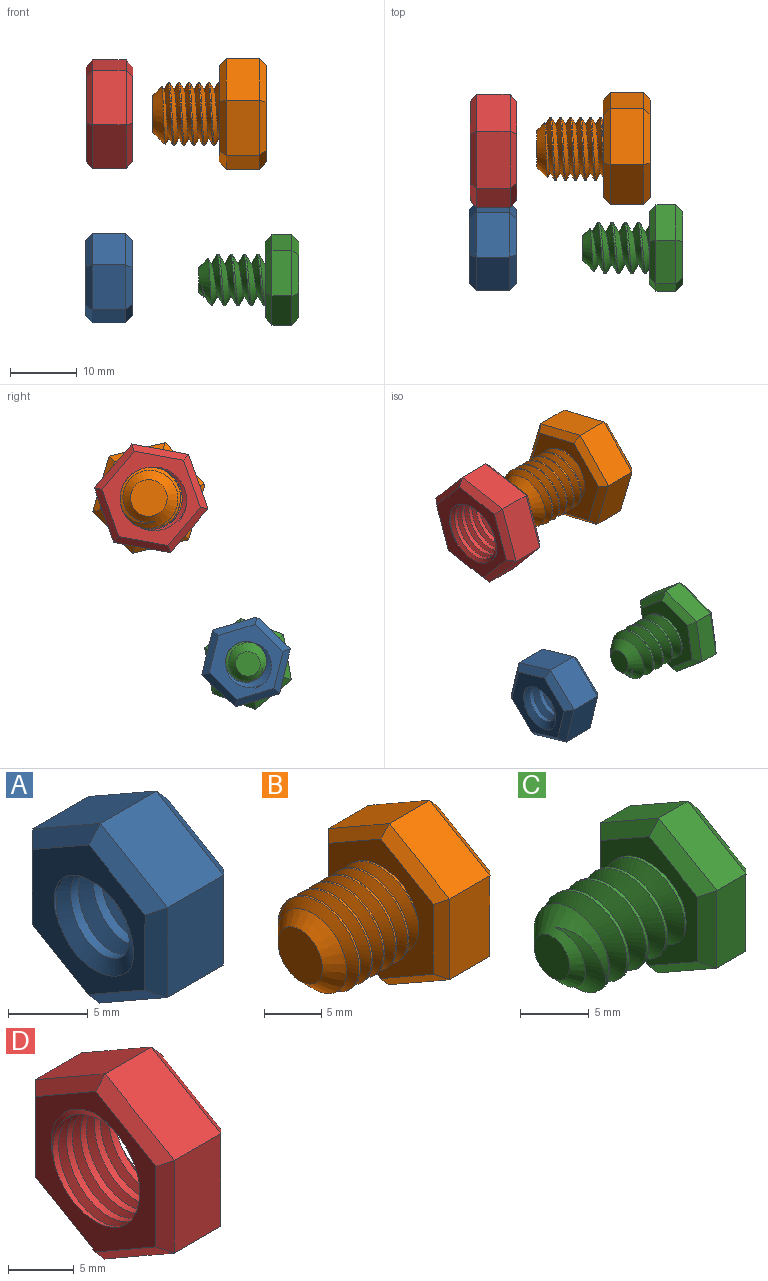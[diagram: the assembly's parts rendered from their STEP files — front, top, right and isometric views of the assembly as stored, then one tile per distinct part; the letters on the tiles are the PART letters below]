
ASSEMBLY  parts=4 mates=2
PART A: 23 faces, bbox 9.2x12.6x14.4 mm
  f0: cylinder r=3.08mm len=7mm, axis (1,0,0), area 47.4mm2, adj f7,f8,f21,f22
  f1: plane 6.02x5mm, normal (0,0.5,0.87), area 34.6mm2, adj f2,f6,f13,f20
  f2: plane 5.98x5mm, normal (0,-0.5,0.86), area 34.6mm2, adj f1,f3,f14,f18
  f3: plane 6.93x5mm, normal (0,-1,-0.01), area 34.6mm2, adj f2,f4,f12,f16
  f4: plane 6.02x5mm, normal (0,-0.5,-0.87), area 34.6mm2, adj f3,f5,f10,f15
  f5: plane 5.98x5mm, normal (0,0.5,-0.86), area 34.6mm2, adj f4,f6,f9,f17
  f6: plane 6.93x5mm, normal (0,1,0.01), area 34.6mm2, adj f1,f5,f11,f19
  f7: plane 12.14x10.62mm, normal (-1,0,0), area 48.9mm2, adj f0,f9,f10,f11,f12,f13,f14,f21
  f8: plane 12.14x10.62mm, normal (1,0,0), area 48.9mm2, adj f0,f15,f16,f17,f18,f19,f20,f21
  f9: plane 5.99x4.07mm, normal (-0.71,0.36,-0.61), area 9mm2, adj f5,f7,f10,f11
  f10: plane 6.02x4.02mm, normal (-0.71,-0.35,-0.61), area 9mm2, adj f4,f7,f9,f12
  f11: plane 6.93x1.03mm, normal (-0.71,0.71,0), area 9mm2, adj f6,f7,f9,f13
  f12: plane 6.93x1.03mm, normal (-0.71,-0.71,0), area 9mm2, adj f3,f7,f10,f14
  f13: plane 6.02x4.02mm, normal (-0.71,0.35,0.61), area 9mm2, adj f1,f7,f11,f14
  f14: plane 5.99x4.07mm, normal (-0.71,-0.36,0.61), area 9mm2, adj f2,f7,f12,f13
  f15: plane 6.02x4.02mm, normal (0.71,-0.35,-0.61), area 9mm2, adj f4,f8,f16,f17
  f16: plane 6.93x1.03mm, normal (0.71,-0.71,0), area 9mm2, adj f3,f8,f15,f18
  f17: plane 5.99x4.07mm, normal (0.71,0.36,-0.61), area 9mm2, adj f5,f8,f15,f19
  f18: plane 5.99x4.07mm, normal (0.71,-0.36,0.61), area 9mm2, adj f2,f8,f16,f20
  f19: plane 6.93x1.03mm, normal (0.71,0.71,0), area 9mm2, adj f6,f8,f17,f20
  f20: plane 6.02x4.02mm, normal (0.71,0.35,0.61), area 9mm2, adj f1,f8,f18,f19
  f21: bspline ~9.71x8.65mm, area 104.3mm2, adj f0,f7,f8,f22
  f22: bspline ~9.71x8.41mm, area 104.3mm2, adj f0,f7,f8,f21
PART B: 25 faces, bbox 17.8x15.9x18.1 mm
  f0: cylinder r=4.75mm len=9.5mm, axis (1,0,0), area 28.1mm2, adj f1,f2,f4,f12
  f1: bspline ~10.97x9.91mm, area 196.7mm2, adj f0,f2,f4,f12
  f2: bspline ~10.97x10.66mm, area 196.6mm2, adj f0,f1,f4,f12
  f3: plane 5.5x5.5mm, normal (-1,0,0), area 23.8mm2, adj f4
  f4: cone r=4.75mm half-angle=45deg, axis (1,0,0), area 47.4mm2, adj f0,f1,f2,f3
  f5: plane 7.48x5mm, normal (0,-0.5,0.86), area 43.3mm2, adj f6,f10,f18,f22
  f6: plane 8.66x5mm, normal (0,-1,0), area 43.3mm2, adj f5,f7,f16,f20
  f7: plane 7.52x5mm, normal (0,-0.5,-0.87), area 43.3mm2, adj f6,f8,f14,f19
  f8: plane 7.48x5mm, normal (0,0.5,-0.86), area 43.3mm2, adj f7,f9,f13,f21
  f9: plane 8.66x5mm, normal (0,1,0), area 43.3mm2, adj f8,f10,f15,f23
  f10: plane 7.52x5mm, normal (0,0.5,0.87), area 43.3mm2, adj f5,f9,f17,f24
  f11: plane 15.01x13.03mm, normal (1,0,0), area 146.4mm2, adj f13,f14,f15,f16,f17,f18
  f12: plane 15.83x13.85mm, normal (-1,0,0), area 89.2mm2, adj f0,f1,f2,f19,f20,f21,f22,f23
  f13: plane 7.49x4.93mm, normal (0.71,0.36,-0.61), area 11.4mm2, adj f8,f11,f14,f15
  f14: plane 7.52x4.88mm, normal (0.71,-0.35,-0.61), area 11.4mm2, adj f7,f11,f13,f16
  f15: plane 8.66x1.03mm, normal (0.71,0.71,0), area 11.4mm2, adj f9,f11,f13,f17
  f16: plane 8.66x1.03mm, normal (0.71,-0.71,0), area 11.4mm2, adj f6,f11,f14,f18
  f17: plane 7.52x4.88mm, normal (0.71,0.35,0.61), area 11.4mm2, adj f10,f11,f15,f18
  f18: plane 7.49x4.93mm, normal (0.71,-0.36,0.61), area 11.4mm2, adj f5,f11,f16,f17
  f19: plane 7.52x4.88mm, normal (-0.71,-0.35,-0.61), area 11.4mm2, adj f7,f12,f20,f21
  f20: plane 8.66x1.03mm, normal (-0.71,-0.71,0), area 11.4mm2, adj f6,f12,f19,f22
  f21: plane 7.49x4.93mm, normal (-0.71,0.36,-0.61), area 11.4mm2, adj f8,f12,f19,f23
  f22: plane 7.49x4.93mm, normal (-0.71,-0.36,0.61), area 11.4mm2, adj f5,f12,f20,f24
  f23: plane 8.66x1.03mm, normal (-0.71,0.71,0), area 11.4mm2, adj f9,f12,f21,f24
  f24: plane 7.52x4.88mm, normal (-0.71,0.35,0.61), area 11.4mm2, adj f10,f12,f22,f23
PART C: 25 faces, bbox 16.7x13.1x14.9 mm
  f0: cylinder r=3.84mm len=8mm, axis (1,0,0), area 24.7mm2, adj f1,f2,f4,f12
  f1: bspline ~10.88x8.87mm, area 148mm2, adj f0,f2,f4,f12
  f2: bspline ~11.88x8.87mm, area 147.9mm2, adj f0,f1,f4,f12
  f3: plane 3.68x3.68mm, normal (-1,0,0), area 10.6mm2, adj f4
  f4: cone r=3.84mm half-angle=45deg, axis (1,0,0), area 30.8mm2, adj f0,f1,f2,f3
  f5: plane 5.98x3.5mm, normal (0,-0.51,0.86), area 20.8mm2, adj f6,f10,f18,f22
  f6: plane 6.93x3mm, normal (0,-1,-0.01), area 20.8mm2, adj f5,f7,f16,f20
  f7: plane 6.02x3.43mm, normal (0,-0.49,-0.87), area 20.8mm2, adj f6,f8,f14,f19
  f8: plane 5.98x3.5mm, normal (0,0.51,-0.86), area 20.8mm2, adj f7,f9,f13,f21
  f9: plane 6.93x3mm, normal (0,1,0.01), area 20.8mm2, adj f8,f10,f15,f23
  f10: plane 6.02x3.43mm, normal (0,0.49,0.87), area 20.8mm2, adj f5,f9,f17,f24
  f11: plane 11.55x10.03mm, normal (1,0,0), area 86.6mm2, adj f13,f14,f15,f16,f17,f18
  f12: plane 12.56x11.04mm, normal (-1,0,0), area 54.2mm2, adj f0,f1,f2,f19,f20,f21,f22,f23
  f13: plane 5.99x4.07mm, normal (0.71,0.36,-0.61), area 9mm2, adj f8,f11,f14,f15
  f14: plane 6.02x4.01mm, normal (0.71,-0.35,-0.61), area 9mm2, adj f7,f11,f13,f16
  f15: plane 6.93x1.04mm, normal (0.71,0.71,0), area 9mm2, adj f9,f11,f13,f17
  f16: plane 6.93x1.04mm, normal (0.71,-0.71,0), area 9mm2, adj f6,f11,f14,f18
  f17: plane 6.02x4.01mm, normal (0.71,0.35,0.61), area 9mm2, adj f10,f11,f15,f18
  f18: plane 5.99x4.07mm, normal (0.71,-0.36,0.61), area 9mm2, adj f5,f11,f16,f17
  f19: plane 6.02x4.01mm, normal (-0.71,-0.35,-0.61), area 9mm2, adj f7,f12,f20,f21
  f20: plane 6.93x1.04mm, normal (-0.71,-0.71,0), area 9mm2, adj f6,f12,f19,f22
  f21: plane 5.99x4.07mm, normal (-0.71,0.36,-0.61), area 9mm2, adj f8,f12,f19,f23
  f22: plane 5.99x4.07mm, normal (-0.71,-0.36,0.61), area 9mm2, adj f5,f12,f20,f24
  f23: plane 6.93x1.04mm, normal (-0.71,0.71,0), area 9mm2, adj f9,f12,f21,f24
  f24: plane 6.02x4.01mm, normal (-0.71,0.35,0.61), area 9mm2, adj f10,f12,f22,f23
PART D: 23 faces, bbox 9.1x15.4x17.7 mm
  f0: plane 7.49x5mm, normal (0,-0.5,0.86), area 43.3mm2, adj f1,f5,f13,f17
  f1: plane 8.66x5mm, normal (0,-1,0), area 43.3mm2, adj f0,f2,f11,f15
  f2: plane 7.51x5mm, normal (0,-0.5,-0.87), area 43.3mm2, adj f1,f3,f9,f14
  f3: plane 7.49x5mm, normal (0,0.5,-0.86), area 43.3mm2, adj f2,f4,f8,f16
  f4: plane 8.66x5mm, normal (0,1,0), area 43.3mm2, adj f3,f5,f10,f18
  f5: plane 7.51x5mm, normal (0,0.5,0.87), area 43.3mm2, adj f0,f4,f12,f19
  f6: plane 15.37x13.38mm, normal (-1,0,0), area 71.4mm2, adj f8,f9,f10,f11,f12,f13,f20,f21
  f7: plane 15.37x13.38mm, normal (1,0,0), area 71.4mm2, adj f14,f15,f16,f17,f18,f19,f20,f21
  f8: plane 7.49x4.93mm, normal (-0.71,0.36,-0.61), area 11.4mm2, adj f3,f6,f9,f10
  f9: plane 7.51x4.89mm, normal (-0.71,-0.35,-0.61), area 11.4mm2, adj f2,f6,f8,f11
  f10: plane 8.66x1.02mm, normal (-0.71,0.71,0), area 11.4mm2, adj f4,f6,f8,f12
  f11: plane 8.66x1.02mm, normal (-0.71,-0.71,0), area 11.4mm2, adj f1,f6,f9,f13
  f12: plane 7.51x4.89mm, normal (-0.71,0.35,0.61), area 11.4mm2, adj f5,f6,f10,f13
  f13: plane 7.49x4.93mm, normal (-0.71,-0.36,0.61), area 11.4mm2, adj f0,f6,f11,f12
  f14: plane 7.51x4.89mm, normal (0.71,-0.35,-0.61), area 11.4mm2, adj f2,f7,f15,f16
  f15: plane 8.66x1.02mm, normal (0.71,-0.71,0), area 11.4mm2, adj f1,f7,f14,f17
  f16: plane 7.49x4.93mm, normal (0.71,0.36,-0.61), area 11.4mm2, adj f3,f7,f14,f18
  f17: plane 7.49x4.93mm, normal (0.71,-0.36,0.61), area 11.4mm2, adj f0,f7,f15,f19
  f18: plane 8.66x1.02mm, normal (0.71,0.71,0), area 11.4mm2, adj f4,f7,f16,f19
  f19: plane 7.51x4.89mm, normal (0.71,0.35,0.61), area 11.4mm2, adj f5,f7,f17,f18
  f20: cylinder r=4.66mm len=9.32mm, axis (1,0,0), area 85.4mm2, adj f6,f7,f21,f22
  f21: bspline ~12.5x10.82mm, area 128.4mm2, adj f6,f7,f20,f22
  f22: bspline ~12.5x10.82mm, area 128.5mm2, adj f6,f7,f20,f21
PLACE A rot(axis=(0,0.6,-0.8),180deg) t=(-55.27,-6.86,23.48)mm fixed
PLACE B rot(axis=(-1,0,0),43.8deg) t=(-31.66,7.73,48.08)mm
PLACE C rot(axis=(1,0,0),109.9deg) t=(-25.77,-7.14,23.19)mm
PLACE D rot(axis=(1,0,0),100.2deg) t=(-48.16,7.38,48.02)mm fixed
MATE cylindrical C.f0 <-> A.f7  axis (-1,0,0) through (-38.27,-7.14,23.19)mm
MATE cylindrical B.f0 <-> D.f6  axis (-1,0,0) through (-45.16,7.73,48.08)mm
